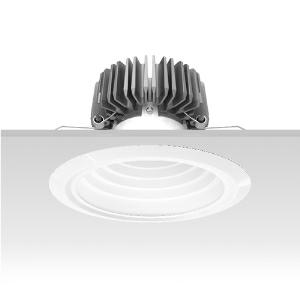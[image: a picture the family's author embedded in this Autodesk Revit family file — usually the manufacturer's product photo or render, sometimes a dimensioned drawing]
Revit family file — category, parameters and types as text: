
# Revit family: 3f_filippi_-_3f_reno_bianco_ampio_3f_filippi_-_30637_a01025_-_3f_reno_200_wh_4000-840_wide___vt_wh_56ca
name_source: partatom
category: Lighting Fixtures
units: mm (PartAtom-declared; Revit-internal decimal feet)

## family parameters
Cut with Voids When Loaded = No
Host = Face
Light Source = No
Part Type = Normal
Room Calculation Point = No
Round Connector Dimension = Use Diameter
Shared = No

## types (1)
- 3F Filippi - 3F Reno Bianco Ampio (1 x LED, 3379 lm, 36 W, 4000 K)
    Apparent Load = 36 VA
    Approval mark = CE
    CIE Flux Codes = 75 94 99 100 100
    Color Rendering = 80
    Color Temperature = 4000 K
    Control Gear = Electronic ballast
    Default Elevation = 1800 mm
    Description = ILLUMINOTECHNICAL
Luminous efficiency 100% (DLOR 100%, ULOR 0%).
Initial luminous flux of the luminaire 3379 lm.
Direct symmetric wide distribution.
Installation Interdistance Transv.D = 1.56 x hu - Long.D = 1.56 x hu.
Tabular UGR (CIE 117 - 4H-8H; S=0.25H; 70/50/20): RUG 22.8 - 22.7.
Beam angle: 74° - 74°.
Luminous efficacy 94 lm/W.
Lifetime (L90/B10): 30000 h. (tq+25°C)
Lifetime (L85/B10): 50000 h. (tq+25°C)
Lifetime (L70/B10): 80000 h. (tq+25°C)
Sudden decreased luminous flux after 50000 hours: 0% (C0).
Photobiological safety in compliance with IEC/TR 62778: RG1 low risk, (IEC 62471).
In compliance with IEC/EN 62722-2-1 - IEC/EN 62717 standards.

SOURCE
Compact LED module 4000/840.
Energy efficiency class (UE 2019/2020 - UE 2019/2015): E.
CIE 13.3 Colour rendering index: CRI >80 (R9 <50%).
IES TM-30 Fidelity Index: Rf = 84 Rg = 95.
CCT nominal colour temperature 4000 K.
Colour initial tolerance (MacAdam): SDCM 3.
Zhaga Book 3 compliant.

MECHANICAL
Passive heat dissipator in die-casting aluminium, oversized, for optimum thermal management of the LED module.
Parabolic element with graduated/concentric rings in white polycarbonate.
Transparent external lens with glossy and satin differentiated surfaces, with a cooling and anti-insect system in methacrylate (PMMA).
Fastening spring clips in stainless steel.
Dimensions: diameter 226 mm, height 146 mm. Weight 1.715 kg.
IP44 protection degree for exposed part, IP20 for recessed part.
Mechanical strength to impacts IK06 (1 joule).
Glow-wire test resistance 650°C.

ELECTRICAL
Wiring on a separate unit.
Halogen Free electronic wiring 230V-50/60Hz, power factor 0.95, THD <25%, constant output current, SELV, class II, 1 driver.
Power of the luminaire 36 W.
ENEC - CE.
SAFE FLICKER: PstLM=<1 and SVM=<0.4 (IEC TR 61547-1 and IEC TR 63158), to ensure a more comfortable and safe light.
Luminaire compliant with EN 60598-2-22 for power supply from a centralised emergency system CPSS (Central Power Supply System), not incorporated in the luminaire - high risk areas excluded. The default power and flux are 100% in AC and 100% in DC.
Ambient temperature from 0°C to +25°C.
Temperature class T6 max 85°C.
Relative humidity UR: <85%.

INSTALLATION
Pull-up recessed fitting.
False ceiling carving: 200 mm.
All accessories dedicated to this product are available on the Catalog and on our website www.3F-Filippi.com.

ACCESSORIES
A01025 - VT transparent glass, tempered, not flammable, locked and in line with the trim, in white polycarbonate.

APPLICATIONS
Environments: architectural, commercial, exhibition areas, transit areas, corridors, shops, display windows, service areas.
In false ceilings with narrow voids.

WARNING
Luminaire designed for disposal/recycling at end-of-life.
Replaceable (LED only) light source by a professional. Replaceable control gear by a professional.
    Height = 0 mm  [stored 0 ft]
    Lamp = 1 x LED
    Lamp Light Flux = 3379 lm
    Lamp Power = 36 W
    Lamp count = 1
    Length = 226 mm
    Lifetime = 50000 h
    Luminous efficacy = 94 lm/W
    Manufacturer = 3F Filippi
    ModVariant = No
    Model = 3F Filippi - 30637+A01025 - 3F Reno 200 WH 4000-840 WIDE + VT WH
    Mounting Place = Ceiling
    Mounting Type = Recessed
    Number of Poles = 1
    OnlyDefault = Yes
    Power Factor = 1
    Product Name = 3F Filippi - 3F Reno Bianco Ampio
    Product group = recessed luminaire
    ProductGroupID = 4
    Protection Class = Protection class II
    Protection Degree = IP 20
    RLX_Detail_Level = 1
    RLX_Emergency_Light_Flux = 0 lm
    RLX_Emergency_Type = 0
    RLX_Emergency_Type_DB = No
    RlxData = <blob elided: 95301 chars, md5=19bc9436>
    Socket = socket
    Standby Power = 0 W
    System Light Flux = 3379 lm
    System Power = 36 W
    Type Comments = Product without accessories
    Type Image = 3ffilippi_3f_reno_200_wh__a01025.jpg
    URL = http://relux.com
    VarID = ---
    Voltage = 0 V
    Weight = 0.00 kg
    Width = 0 mm  [stored 0 ft]

note: [stored X ft] marks values corroborated as IEEE doubles in the binary element streams (Revit-internal decimal feet)

## geometry (parser evidence)
native form markers: Blend x4, Sweep x9
no freeform markers — native parametric forms only
